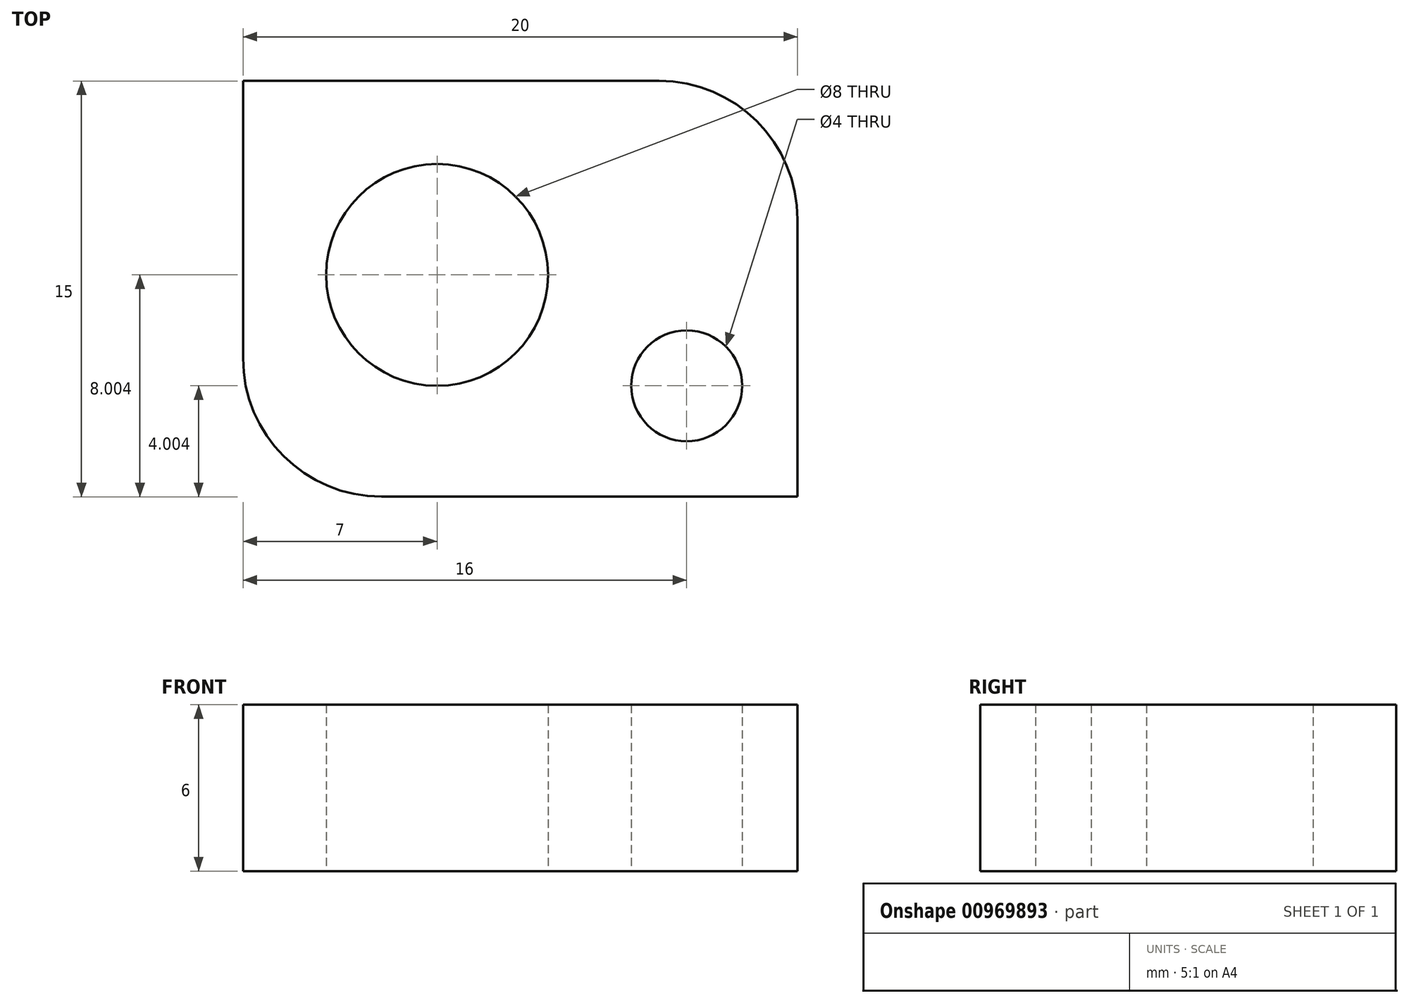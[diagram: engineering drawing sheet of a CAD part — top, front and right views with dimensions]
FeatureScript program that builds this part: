
annotation { "Feature Type Name" : "Feature", "Feature Type Description" : "" }
export const myFeature = defineFeature(function(context is Context, id is Id, definition is map)
    precondition{}
    {
        {
            var Q0;
            Q0=qCreatedBy(makeId("Top.planeOp"),FACE);
            var sketch = newSketch(context, id + "F0", { "sketchPlane" : qUnion([Q0])});
            skLineSegment(sketch, "E0.bottom", {"start": v(-66.68, -12.46) * mm, "end": v(-46.68, -12.46) * mm});
            skLineSegment(sketch, "E0.top", {"start": v(-66.68, -27.46) * mm, "end": v(-46.68, -27.46) * mm});
            skLineSegment(sketch, "E0.left", {"start": v(-66.68, -12.46) * mm, "end": v(-66.68, -27.46) * mm});
            skLineSegment(sketch, "E0.right", {"start": v(-46.68, -12.46) * mm, "end": v(-46.68, -27.46) * mm});
            skCircle(sketch, "E1", {"center": v(-59.68, -19.46) * mm, "radius": 4 * mm});
            skCircle(sketch, "E2", {"center": v(-50.68, -23.46) * mm, "radius": 2 * mm});
            skSolve(sketch);
        }
        {
            var Q0;
            Q0=makeQuery(id+"F0.imprint","IMPRINT",FACE,{"disambiguationData":[TD([[makeQuery(id+"F0.imprint","IMPRINT",EDGE,{"derivedFrom":sQuery(id+"F0.wireOp",EDGE,"E0.bottom")}),-1.0]])]});
            extrude(context, id + "F1", {"entities" : qUnion([Q0]), "depth" : 6 * mm, "offsetDistance" : 25 * mm});
        }
        {
            var Q0;
            Q0=makeQuery(id+"F1.opExtrude","SWEPT_EDGE",EDGE,{"disambiguationData":[OSD([sQuery(id+"F0.wireOp",EDGE,"E0.bottom"),sQuery(id+"F0.wireOp",EDGE,"E0.right")])]});
            var Q1;
            Q1=makeQuery(id+"F1.opExtrude","SWEPT_EDGE",EDGE,{"disambiguationData":[OSD([sQuery(id+"F0.wireOp",EDGE,"E0.top"),sQuery(id+"F0.wireOp",EDGE,"E0.left")])]});
            fillet(context, id + "F2", {"entities" : qUnion([Q0, Q1]), "radius" : 5 * mm, "tangentPropagation" : true, "allowEdgeOverflow" : false});
        }
    });
